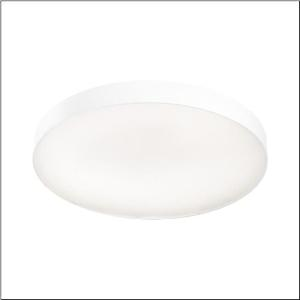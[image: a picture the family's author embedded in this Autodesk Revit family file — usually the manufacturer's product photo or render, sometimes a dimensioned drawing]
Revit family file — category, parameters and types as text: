
# Revit family: round_21_l_51mr38nd0321w
name_source: partatom
category: Lighting Fixtures
units: mm (PartAtom-declared; Revit-internal decimal feet)

## family parameters
Cut with Voids When Loaded = No
Host = Face
Light Source = No
Part Type = Normal
Room Calculation Point = No
Round Connector Dimension = Use Diameter
Shared = No

## types (1)
- Round 21 L (1 x LED, 11740 lm, 88.2 W, 3000K)
    Apparent Load = 88 VA
    CIE Flux Codes = 66 90 98 71 100
    Color Rendering = 80
    Color Temperature = 3000K
    Default Elevation = 1800 mm
    Description = Round 21 L, wall and ceiling luminaire, primary optical cover: micro prismatic cover, of PMMA, transparent, CAT 2 (L<= 3000cd/m²), light emission: direct/indirect distribution, primary light characteristic: symmetric, installation type: suspended mounting, surface-mounted, LED, rated luminous flux: 9.230lm, luminous efficacy: 111lm/W, light colour: 830, colour temperature: 3000K, with terminal, 5-pole, mains connection: 230V, AC, 50/60Hz, rated input power: 83W, housing, of aluminium, coated, white, diameter: 850mm, height: 62mm, protection rating (complete): IP40, insulation class (complete): insulation class I (protective earthing), certification: CE, impact resistance: IK04, permissible operating ambient temperature: -10..+35°C, packaging unit: 1 piece
    Height = 87 mm
    Lamp = 1 x LED
    Lamp Light Flux = 11740 lm
    Lamp Power = 88.2 W
    Lamp count = 1
    Length = 850 mm
    Luminous efficacy = 133 lm/W
    Manufacturer = Siteco
    ModVariant = No
    Model = 51MR38ND0321W
    Mounting Place = Ceiling
    Mounting Type = Surface mounted
    Number of Poles = 1
    OnlyDefault = Yes
    Power Factor = 1
    Product Name = Round 21 L
    Product group = wall and ceiling luminaire
    ProductGroupID = 303
    Protection Class = Protection class I
    Protection Degree = IP 40
    RLX_Detail_Level = 1
    RLX_Emergency_Light_Flux = 0 lm
    RLX_Emergency_Type = 0
    RLX_Emergency_Type_DB = No
    RlxData = <blob elided: 19509 chars, md5=db65f392>
    Socket = socket
    Standby Power = 0 W
    System Light Flux = 11740 lm
    System Power = 88 W
    Type Comments = Product without accessories
    Type Image = l_1258318.jpg
    URL = http://relux.com
    VarID = ---
    Voltage = 0 V
    Weight = 0.00 kg
    Width = 0 mm  [stored 0 ft]

note: [stored X ft] marks values corroborated as IEEE doubles in the binary element streams (Revit-internal decimal feet)

## geometry (parser evidence)
native form markers: Blend x4, Sweep x15
no freeform markers — native parametric forms only
